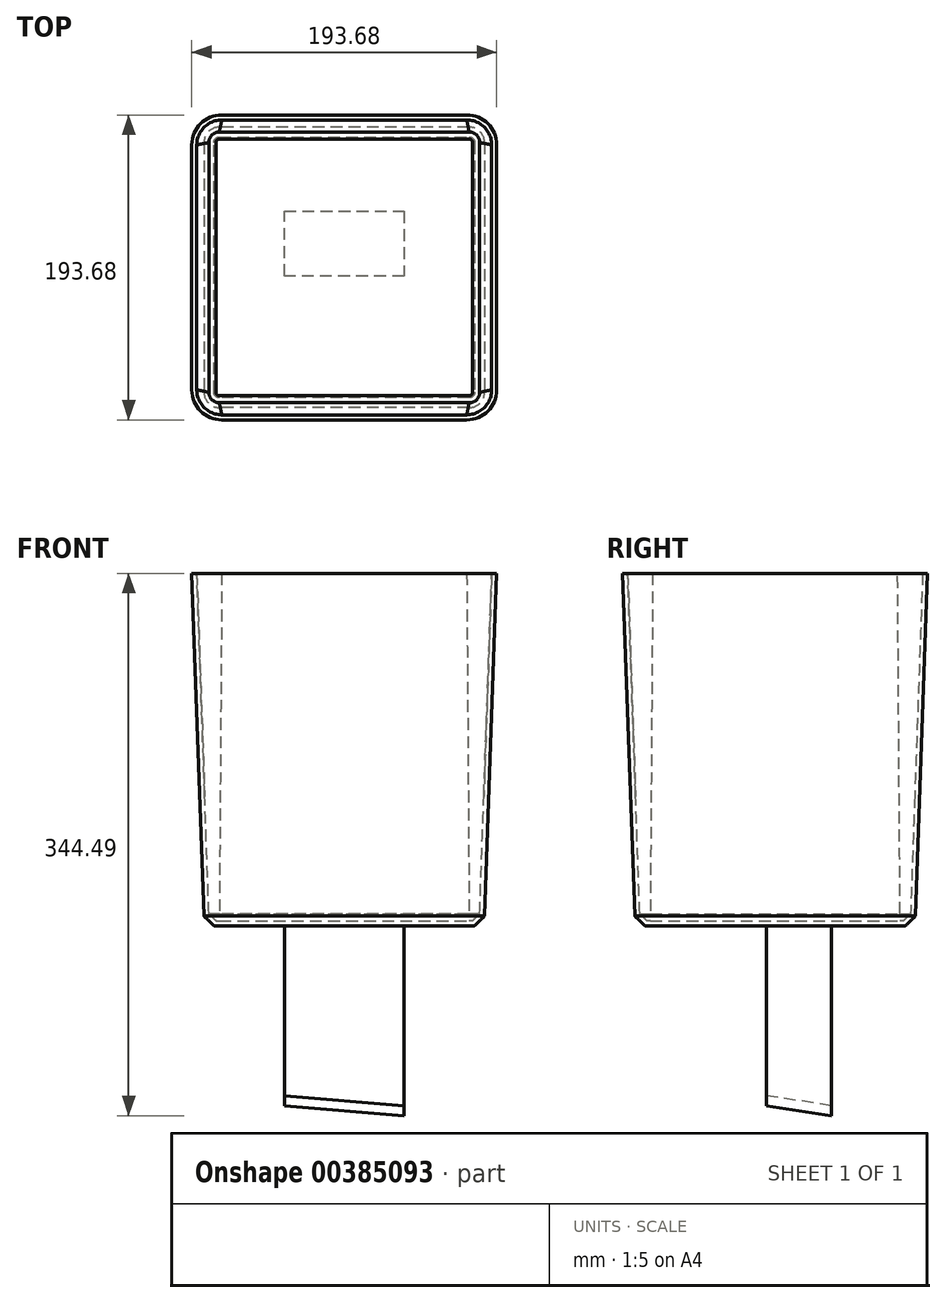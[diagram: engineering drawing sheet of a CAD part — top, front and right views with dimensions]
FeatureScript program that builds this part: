
annotation { "Feature Type Name" : "Feature", "Feature Type Description" : "" }
export const myFeature = defineFeature(function(context is Context, id is Id, definition is map)
    precondition{}
    {
        {
            var Q0;
            Q0=qCreatedBy(makeId("Top.planeOp"),FACE);
            var sketch = newSketch(context, id + "F0", { "sketchPlane" : qUnion([Q0])});
            skLineSegment(sketch, "E0.bottom", {"start": v(79.38, 88.9) * mm, "end": v(-79.38, 88.9) * mm});
            skLineSegment(sketch, "E0.top", {"start": v(79.37, -88.9) * mm, "end": v(-79.38, -88.9) * mm});
            skLineSegment(sketch, "E0.left", {"start": v(88.9, 79.38) * mm, "end": v(88.9, -79.38) * mm});
            skLineSegment(sketch, "E0.right", {"start": v(-88.9, 79.38) * mm, "end": v(-88.9, -79.38) * mm});
            skPoint(sketch, "E0.middle", {"position": v(0, 0) * mm});
            skPoint(sketch, "E1.visualSharp", {"position": v(-88.9, 88.9) * mm});
            skArc(sketch, "E1.filletArc", {"start": v(-79.38, 88.9) * mm, "mid": v(-86.11, 86.11) * mm, "end": v(-88.9, 79.38) * mm});
            skPoint(sketch, "E2.visualSharp", {"position": v(-88.9, -88.9) * mm});
            skArc(sketch, "E2.filletArc", {"start": v(-88.9, -79.38) * mm, "mid": v(-86.11, -86.11) * mm, "end": v(-79.38, -88.9) * mm});
            skPoint(sketch, "E3.visualSharp", {"position": v(88.9, -88.9) * mm});
            skArc(sketch, "E3.filletArc", {"start": v(79.37, -88.9) * mm, "mid": v(86.11, -86.11) * mm, "end": v(88.9, -79.38) * mm});
            skPoint(sketch, "E4.visualSharp", {"position": v(88.9, 88.9) * mm});
            skArc(sketch, "E4.filletArc", {"start": v(88.9, 79.38) * mm, "mid": v(86.11, 86.11) * mm, "end": v(79.38, 88.9) * mm});
            skSolve(sketch);
        }
        {
            var Q0;
            Q0=qCreatedBy(makeId("Top.planeOp"),FACE);
            cPlane(context, id + "F1", {"entities" : qUnion([Q0]), "cplaneType" : CPlaneType.OFFSET, "offset" : 223.84 * mm, "width" : 152.4 * mm, "height" : 152.4 * mm});
        }
        {
            var Q0;
            Q0=qCreatedBy(id+"F1.planeOp",FACE);
            var sketch = newSketch(context, id + "F2", { "sketchPlane" : qUnion([Q0])});
            skLineSegment(sketch, "E5.bottom", {"start": v(77.79, 96.84) * mm, "end": v(-77.79, 96.84) * mm});
            skLineSegment(sketch, "E5.top", {"start": v(77.79, -96.84) * mm, "end": v(-77.79, -96.84) * mm});
            skLineSegment(sketch, "E5.left", {"start": v(96.84, 77.79) * mm, "end": v(96.84, -77.79) * mm});
            skLineSegment(sketch, "E5.right", {"start": v(-96.84, 77.79) * mm, "end": v(-96.84, -77.79) * mm});
            skPoint(sketch, "E5.middle", {"position": v(0, 0) * mm});
            skPoint(sketch, "E6.visualSharp", {"position": v(96.84, 96.84) * mm});
            skArc(sketch, "E6.filletArc", {"start": v(96.84, 77.79) * mm, "mid": v(91.26, 91.26) * mm, "end": v(77.79, 96.84) * mm});
            skPoint(sketch, "E7.visualSharp", {"position": v(-96.84, 96.84) * mm});
            skArc(sketch, "E7.filletArc", {"start": v(-77.79, 96.84) * mm, "mid": v(-91.26, 91.26) * mm, "end": v(-96.84, 77.79) * mm});
            skPoint(sketch, "E8.visualSharp", {"position": v(-96.84, -96.84) * mm});
            skArc(sketch, "E8.filletArc", {"start": v(-96.84, -77.79) * mm, "mid": v(-91.26, -91.26) * mm, "end": v(-77.79, -96.84) * mm});
            skPoint(sketch, "E9.visualSharp", {"position": v(96.84, -96.84) * mm});
            skArc(sketch, "E9.filletArc", {"start": v(77.79, -96.84) * mm, "mid": v(91.26, -91.26) * mm, "end": v(96.84, -77.79) * mm});
            skSolve(sketch);
        }
        {
            var Q0;
            Q0=makeQuery(id+"F0.imprint","IMPRINT",FACE,{"disambiguationData":[TD([[makeQuery(id+"F0.imprint","IMPRINT",EDGE,{"derivedFrom":sQuery(id+"F0.wireOp",EDGE,"E0.bottom")}),1.0]])]});
            var Q1;
            Q1=makeQuery(id+"F2.imprint","IMPRINT",FACE,{"disambiguationData":[TD([[makeQuery(id+"F2.imprint","IMPRINT",EDGE,{"derivedFrom":sQuery(id+"F2.wireOp",EDGE,"E5.bottom")}),1.0]])]});
            loft(context, id + "F3", {"sheetProfilesArray" : [{ "sheetProfileEntities" : qUnion([Q0]) }, { "sheetProfileEntities" : qUnion([Q1]) }]});
        }
        {
            var Q0;
            Q0=makeQuery(id+"F3.opLoft","MID_CAP_EDGE",EDGE,{"disambiguationData":[OSD([sQuery(id+"F0.wireOp",EDGE,"E0.bottom"),sQuery(id+"F0.wireOp",EDGE,"E1.filletArc"),sQuery(id+"F0.wireOp",EDGE,"E4.filletArc")])],"capPos":0.0});
            chamfer(context, id + "F4", {"entities" : qUnion([Q0]), "width" : 6.35 * mm, "tangentPropagation" : true});
        }
        {
            var Q0;
            Q0=makeQuery(id+"F3.opLoft","CAP_FACE",FACE,{"disambiguationData":[OSD([makeQuery(id+"F2.imprint","IMPRINT",FACE,{"disambiguationData":[TD([[makeQuery(id+"F2.imprint","IMPRINT",EDGE,{"derivedFrom":sQuery(id+"F2.wireOp",EDGE,"E5.bottom")}),1.0]])]})])],"isStart":true});
            shell(context, id + "F5", {"entities" : qUnion([Q0]), "thickness" : 3.17 * mm});
        }
        {
            var Q0;
            Q0=makeQuery(id+"F3.opLoft","CAP_FACE",FACE,{"disambiguationData":[OSD([makeQuery(id+"F0.imprint","IMPRINT",FACE,{"disambiguationData":[TD([[makeQuery(id+"F0.imprint","IMPRINT",EDGE,{"derivedFrom":sQuery(id+"F0.wireOp",EDGE,"E0.bottom")}),1.0]])]})])],"isStart":true});
            var sketch = newSketch(context, id + "F6", { "sketchPlane" : qUnion([Q0])});
            skCircle(sketch, "E10", {"center": v(0, 0) * mm, "radius": 55.56 * mm});
            skLineSegment(sketch, "E11.1", {"start": v(-38.07, -35.73) * mm, "end": v(38.07, -35.73) * mm});
            skLineSegment(sketch, "E12", {"start": v(38.07, -35.73) * mm, "end": v(38.07, 5.48) * mm});
            skLineSegment(sketch, "E13", {"start": v(38.07, 5.48) * mm, "end": v(-38.07, 5.48) * mm});
            skLineSegment(sketch, "E14", {"start": v(-38.07, 5.48) * mm, "end": v(-38.07, -35.73) * mm});
            skSolve(sketch);
        }
        {
            var Q0;
            Q0=makeQuery(id+"F6.imprint","IMPRINT",FACE,{"disambiguationData":[TD([[makeQuery(id+"F6.imprint","IMPRINT",EDGE,{"derivedFrom":sQuery(id+"F6.wireOp",EDGE,"E11.1")}),1.0]])]});
            extrude(context, id + "F7", {"entities" : qUnion([Q0]), "operationType" : NewBodyOperationType.ADD, "depth" : 120.65 * mm});
        }
        {
            var Q0;
            Q0=makeQuery(id+"F7.opExtrude","SWEPT_FACE",FACE,{"disambiguationData":[OSD([sQuery(id+"F6.wireOp",EDGE,"E13")])]});
            var sketch = newSketch(context, id + "F8", { "sketchPlane" : qUnion([Q0])});
            skLineSegment(sketch, "E15", {"start": v(38.07, -120.65) * mm, "end": v(38.07, -114.3) * mm});
            skLineSegment(sketch, "E16", {"start": v(-38.07, -120.65) * mm, "end": v(-38.07, -107.95) * mm});
            skSolve(sketch);
        }
        {
            var Q0;
            Q0=makeQuery(id+"F7.opExtrude","CAP_VERTEX",VERTEX,{"disambiguationData":[OSD([sQuery(id+"F6.wireOp",EDGE,"E11.1"),sQuery(id+"F6.wireOp",EDGE,"E12")])],"isStart":false});
            var Q1;
            Q1=sQuery(id+"F8.wireOp",VERTEX,"E15.end");
            var Q2;
            Q2=sQuery(id+"F8.wireOp",VERTEX,"E16.end");
            cPlane(context, id + "F9", {"entities" : qUnion([Q0, Q1, Q2]), "cplaneType" : CPlaneType.THREE_POINT, "offset" : 25.4 * mm, "width" : 152.4 * mm, "height" : 152.4 * mm});
        }
        {
            var Q0;
            Q0=qCreatedBy(id+"F9.planeOp",FACE);
            var sketch = newSketch(context, id + "F10", { "sketchPlane" : qUnion([Q0])});
            skLineSegment(sketch, "E17.bottom", {"start": v(-46, -17.81) * mm, "end": v(92.63, -17.81) * mm});
            skLineSegment(sketch, "E17.top", {"start": v(-46, 79.93) * mm, "end": v(92.63, 79.93) * mm});
            skLineSegment(sketch, "E17.left", {"start": v(-46, -17.81) * mm, "end": v(-46, 79.93) * mm});
            skLineSegment(sketch, "E17.right", {"start": v(92.63, -17.81) * mm, "end": v(92.63, 79.93) * mm});
            skSolve(sketch);
        }
        {
            var Q0;
            Q0=makeQuery(id+"F10.imprint","IMPRINT",FACE,{"disambiguationData":[TD([[makeQuery(id+"F10.imprint","IMPRINT",EDGE,{"derivedFrom":sQuery(id+"F10.wireOp",EDGE,"E17.bottom")}),1.0]])]});
            extrude(context, id + "F11", {"entities" : qUnion([Q0]), "oppositeDirection" : true, "depth" : 25.4 * mm});
        }
        {
            var Q0;
            Q0=makeQuery(id+"F11.opExtrude","SWEPT_BODY",BODY,{"disambiguationData":[OSD([sQuery(id+"F10.wireOp",EDGE,"E17.bottom"),sQuery(id+"F10.wireOp",EDGE,"E17.top"),sQuery(id+"F10.wireOp",EDGE,"E17.left"),sQuery(id+"F10.wireOp",EDGE,"E17.right")])]});
            var Q1;
            Q1=makeQuery(id+"F3.opLoft","SWEPT_BODY",BODY,{"disambiguationData":[OSD([makeQuery(id+"F0.imprint","IMPRINT",FACE,{"disambiguationData":[TD([[makeQuery(id+"F0.imprint","IMPRINT",EDGE,{"derivedFrom":sQuery(id+"F0.wireOp",EDGE,"E0.bottom")}),1.0]])]}),makeQuery(id+"F2.imprint","IMPRINT",FACE,{"disambiguationData":[TD([[makeQuery(id+"F2.imprint","IMPRINT",EDGE,{"derivedFrom":sQuery(id+"F2.wireOp",EDGE,"E5.bottom")}),1.0]])]})])]});
            booleanBodies(context, id + "F12", {"operationType" : BooleanOperationType.SUBTRACTION, "tools" : qUnion([Q0]), "targets" : qUnion([Q1])});
        }
    });
